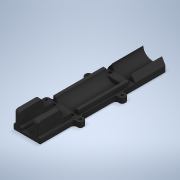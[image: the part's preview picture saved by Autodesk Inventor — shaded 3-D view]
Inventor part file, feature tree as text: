
AUTODESK INVENTOR PART (.ipt)
format: ipt  version: 2020 (Build 240168000, 168)  size: 602,112 bytes
history: native  units: mm
features: projected_geometry x13, sketch x12, extrude x11, fillet x5, hole x2, chamfer x2, plane x1, direct_edit x1, move_body x1
ambient origin geometry x8: Origin, YZ Plane, XZ Plane, XY Plane, X Axis, Y Axis, Z Axis, Center Point
bodies: Solid1 (feature_tree)
feature tree (48):
  extrude  "Extrusion1"  Depth=100.0mm
  plane  "Work Plane1"
  sketch  "Sketch2"  dims[d2=6.0mm d3=0.0mm d4=-7.0mm]
  extrude  "Extrusion2"  [1 undecoded]
  extrude  "Extrusion7"  Depth=21.5mm
  extrude  "Extrusion3"  Depth=51.8mm
  hole  "Hole1"  [1 undecoded]
  direct_edit  "Direct Edit1"
  extrude  "Extrusion4"  Depth=5.0mm
  extrude  "Extrusion5"  Depth=5.0mm
  extrude  "Extrusion6"  Depth=5.0mm
  hole  "Hole2"  [1 undecoded]
  extrude  "Extrusion8"  Depth=3.0mm TaperAngle=0.0deg
  fillet  "Fillet1"  Radius=10.5mm
  fillet  "Fillet2"  Radius=31.0mm
  fillet  "Fillet3"  Radius=3.0mm
  chamfer  "Chamfer1"  Distance=5.0mm
  chamfer  "Chamfer2"  Distance=20.0mm
  fillet  "Fillet4"  Radius=14.0mm
  extrude  "Extrusion9"  Depth=5.0mm
  fillet  "Fillet5"  Radius=7.0mm
  extrude  "Extrusion10"  Depth=5.0mm
  extrude  "Extrusion11"  Depth=5.0mm
  sketch  "Sketch1"  dims[d0=29.0mm d1=100.0mm]
  projected_geometry  "Projected Loop1"
  sketch  "Sketch3"  dims[d5=12.5mm d6=21.5mm]
  projected_geometry  "Projected Loop2"
  sketch  "Sketch4"  dims[d7=51.8mm d8=0.0mm d9=12.5mm]
  projected_geometry  "Projected Loop3"
  sketch  "Sketch5"  dims[d10=20.0mm d11=34.0mm d12=0.0mm]
  projected_geometry  "Projected Loop4"
  sketch  "Sketch6"  dims[d13=3.0mm d14=5.0mm]
  projected_geometry  "Projected Loop5"
  sketch  "Sketch7"  dims[d15=3.0mm d16=5.0mm]
  projected_geometry  "Projected Loop6"
  sketch  "Sketch8"  dims[d17=3.1mm d18=6.0mm d19=5.5mm d20=2.0mm d21=90.0deg d22=6.0mm d23=0.0mm d24=5.0mm]
  projected_geometry  "Projected Loop7"
  sketch  "Sketch9"  dims[d25=63.0mm d26=5.0mm]
  projected_geometry  "Projected Loop8"
  sketch  "Sketch10"  dims[d27=63.0mm d28=0.0mm d29=0.0mm d30=31.0mm d31=10.5mm d32=31.0mm d33=3.0mm d34=0.0mm]
  projected_geometry  "Projected Loop9"
  sketch  "Sketch11"  dims[d35=5.0mm]
  projected_geometry  "Projected Loop10"
  sketch  "Sketch12"  dims[d36=20.0mm d37=5.0mm d38=20.0mm d39=14.0mm d40=0.0mm d41=7.0mm d42=7.0mm d43=7.0mm d44=7.0mm d45=6.0mm d46=0.0mm d47=3.5mm d48=3.5mm d49=3.5mm d50=3.5mm d51=3.1mm d52=6.0mm d53=5.5mm d54=2.0mm d55=90.0deg d56=6.0mm d57=0.0mm d58=31.0mm d59=38.0mm d60=34.0mm d61=6.75mm d62=0.0mm d63=55.0mm d64=176.0mm d65=152.0mm d66=85.25mm d67=0.0mm d68=1.0mm d69=3.0mm d70=3.0mm d71=3.0mm d72=1.0mm d73=4.5mm d74=6.0mm d75=45.0deg d76=4.5mm d77=6.0mm d78=45.0deg d79=1.0mm d80=5.0mm d81=0.0mm d82=3.0mm d83=1.0mm d84=6.1mm d85=27.2mm d87=14.5mm d88=53.8mm d89=0.1mm d90=0.1mm d91=5.0mm d92=0.0mm d93=5.0mm d94=53.75mm d95=0.0mm d96=0.0mm]
  projected_geometry  "Projected Loop11"
  projected_geometry  "Projected Loop12"
  projected_geometry  "Projected Loop13"
  move_body  "Move1"
note: 3 required parameter values undecoded (feature->parameter linkage not recoverable at this tier; creation-order binding heuristic only, values carry confidence <= 0.55)
